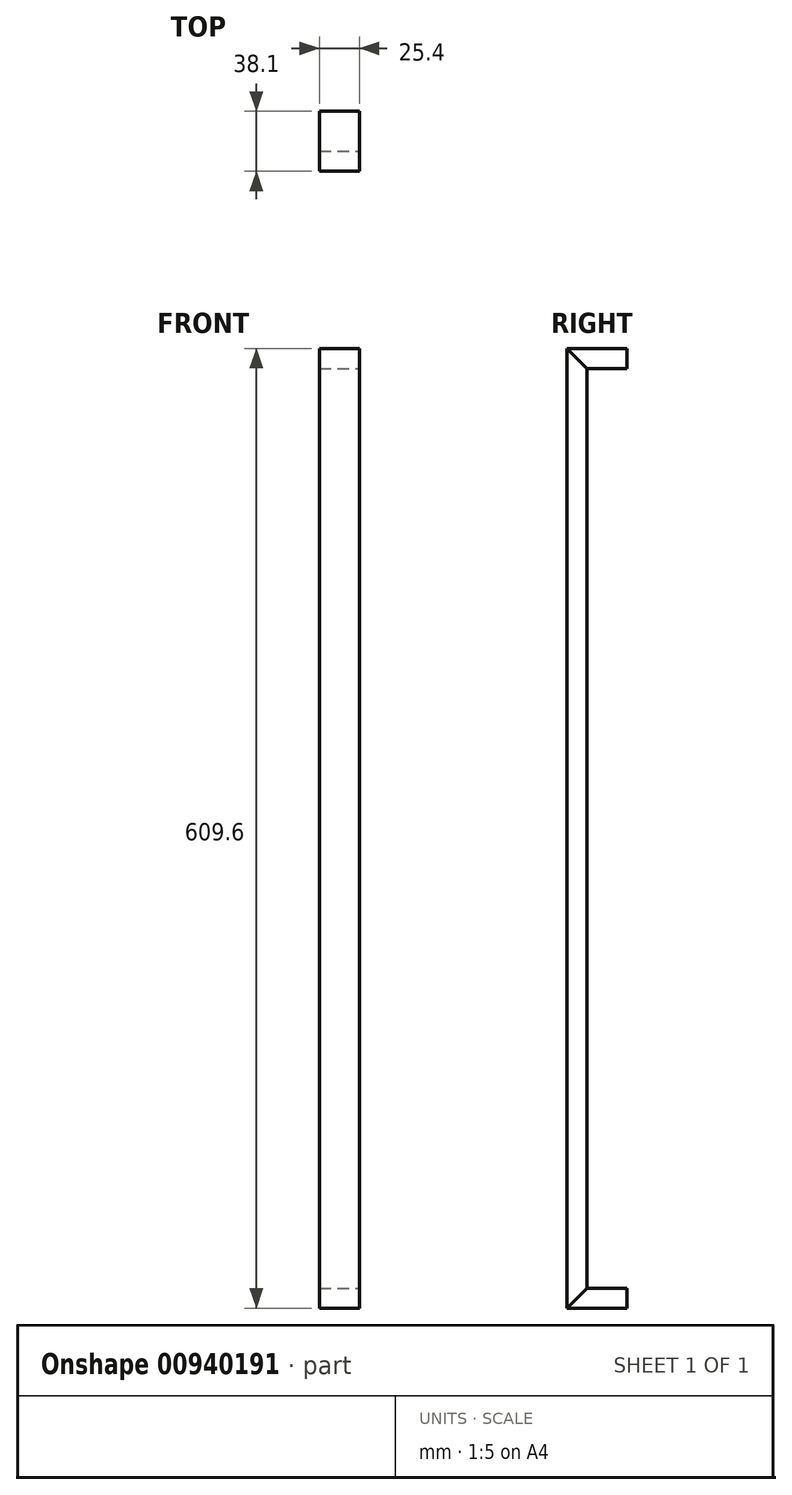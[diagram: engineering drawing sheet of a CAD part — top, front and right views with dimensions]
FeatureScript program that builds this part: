
annotation { "Feature Type Name" : "Feature", "Feature Type Description" : "" }
export const myFeature = defineFeature(function(context is Context, id is Id, definition is map)
    precondition{}
    {
        {
            var Q0;
            Q0=qCreatedBy(makeId("Right.planeOp"),FACE);
            var sketch = newSketch(context, id + "F0", { "sketchPlane" : qUnion([Q0])});
            skLineSegment(sketch, "E0.bottom", {"start": v(-12.7, -292.1) * mm, "end": v(12.7, -292.1) * mm, "construction": true});
            skLineSegment(sketch, "E0.top", {"start": v(-12.7, 292.1) * mm, "end": v(12.7, 292.1) * mm, "construction": true});
            skLineSegment(sketch, "E0.left", {"start": v(-12.7, -292.1) * mm, "end": v(-12.7, 292.1) * mm, "construction": true});
            skLineSegment(sketch, "E0.right", {"start": v(12.7, -292.1) * mm, "end": v(12.7, 292.1) * mm, "construction": true});
            skPoint(sketch, "E0.middle", {"position": v(0, 0) * mm});
            skLineSegment(sketch, "E1.bottom", {"start": v(12.7, 292.1) * mm, "end": v(-12.7, 292.1) * mm});
            skLineSegment(sketch, "E1.top", {"start": v(12.7, 304.8) * mm, "end": v(-12.7, 304.8) * mm});
            skLineSegment(sketch, "E1.left", {"start": v(12.7, 292.1) * mm, "end": v(12.7, 304.8) * mm});
            skLineSegment(sketch, "E1.right", {"start": v(-12.7, 292.1) * mm, "end": v(-12.7, 304.8) * mm});
            skLineSegment(sketch, "E2.bottom", {"start": v(12.7, -292.1) * mm, "end": v(-12.7, -292.1) * mm});
            skLineSegment(sketch, "E2.top", {"start": v(12.7, -304.8) * mm, "end": v(-12.7, -304.8) * mm});
            skLineSegment(sketch, "E2.left", {"start": v(12.7, -292.1) * mm, "end": v(12.7, -304.8) * mm});
            skLineSegment(sketch, "E2.right", {"start": v(-12.7, -292.1) * mm, "end": v(-12.7, -304.8) * mm});
            skLineSegment(sketch, "E3.bottom", {"start": v(-12.7, 304.8) * mm, "end": v(-25.4, 304.8) * mm});
            skLineSegment(sketch, "E3.top", {"start": v(-12.7, -304.8) * mm, "end": v(-25.4, -304.8) * mm});
            skLineSegment(sketch, "E3.left", {"start": v(-12.7, 304.8) * mm, "end": v(-12.7, -304.8) * mm});
            skLineSegment(sketch, "E3.right", {"start": v(-25.4, 304.8) * mm, "end": v(-25.4, -304.8) * mm});
            skLineSegment(sketch, "E4", {"start": v(-12.7, -292.1) * mm, "end": v(-25.4, -304.8) * mm});
            skLineSegment(sketch, "E5", {"start": v(-12.7, 292.1) * mm, "end": v(-25.4, 304.8) * mm});
            skSolve(sketch);
        }
        {
            var Q0;
            {var subQ0=sQuery(id+"F0.wireOp",EDGE,"E1.bottom");Q0=makeQuery(id+"F0.imprint","IMPRINT",FACE,{"disambiguationData":[TD([[makeQuery(id+"F0.imprint","IMPRINT",EDGE,{"derivedFrom":subQ0}),-1.0]])]});}
            var Q1;
            {var subQ0=sQuery(id+"F0.wireOp",EDGE,"E3.bottom");Q1=makeQuery(id+"F0.imprint","IMPRINT",FACE,{"disambiguationData":[TD([[makeQuery(id+"F0.imprint","IMPRINT",EDGE,{"derivedFrom":subQ0}),1.0]])]});}
            var Q2;
            {var subQ0=sQuery(id+"F0.wireOp",EDGE,"E2.bottom");Q2=makeQuery(id+"F0.imprint","IMPRINT",FACE,{"disambiguationData":[TD([[makeQuery(id+"F0.imprint","IMPRINT",EDGE,{"derivedFrom":subQ0}),1.0]])]});}
            var Q3;
            {var subQ0=sQuery(id+"F0.wireOp",EDGE,"E3.top");Q3=makeQuery(id+"F0.imprint","IMPRINT",FACE,{"disambiguationData":[TD([[makeQuery(id+"F0.imprint","IMPRINT",EDGE,{"derivedFrom":subQ0}),-1.0]])]});}
            extrude(context, id + "F1", {"entities" : qUnion([Q0, Q1, Q2, Q3]), "endBound" : BoundingType.SYMMETRIC, "depth" : 25.4 * mm, "offsetDistance" : 25.4 * mm});
        }
        {
            var Q0;
            Q0=makeQuery(id+"F0.imprint","IMPRINT",FACE,{"disambiguationData":[TD([[makeQuery(id+"F0.imprint","IMPRINT",EDGE,{"derivedFrom":sQuery(id+"F0.wireOp",EDGE,"E3.right")}),1.0]])]});
            extrude(context, id + "F2", {"entities" : qUnion([Q0]), "endBound" : BoundingType.SYMMETRIC, "oppositeDirection" : true, "depth" : 25.4 * mm, "offsetDistance" : 25.4 * mm});
        }
    });
